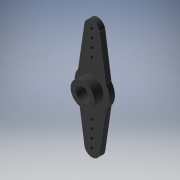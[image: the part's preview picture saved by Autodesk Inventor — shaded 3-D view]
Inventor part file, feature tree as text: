
AUTODESK INVENTOR PART (.ipt)
format: ipt  version: 2019.4 (Build 234330000, 330)  size: 252,928 bytes
history: native  units: mm
features: extrude x7, sketch x6, other x1
ambient origin geometry x8: Origin, YZ Plane, XZ Plane, XY Plane, X Axis, Y Axis, Z Axis, Center Point
bodies: Body1 (feature_tree)
feature tree (14):
  other  "ソリッド1"
  extrude  "押し出し1"  Depth=12.5mm
  extrude  "押し出し2"  Depth=10.0mm
  extrude  "押し出し3"  Depth=10.0mm
  extrude  "押し出し4"  Depth=15.0mm
  extrude  "押し出し5"  Depth=5.5mm
  sketch  "スケッチ6"
  extrude  "押し出し6"  Depth=12.5mm
  extrude  "押し出し7"  Depth=2.0mm TaperAngle=0.0deg
  sketch  "スケッチ1"
  sketch  "スケッチ2"
  sketch  "スケッチ3"
  sketch  "スケッチ4"
  sketch  "スケッチ5"
